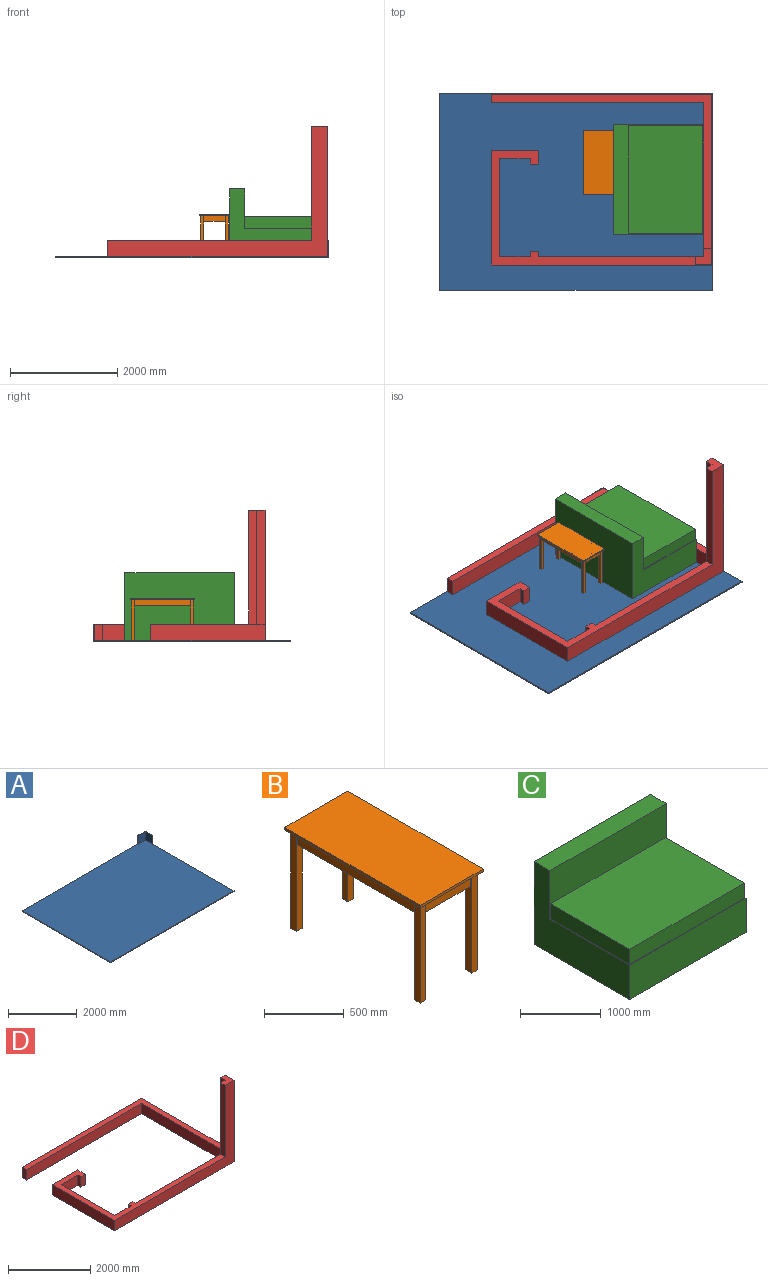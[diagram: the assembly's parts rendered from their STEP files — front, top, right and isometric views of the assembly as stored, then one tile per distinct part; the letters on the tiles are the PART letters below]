
ASSEMBLY  parts=4 mates=7
PART A: 11 faces, bbox 5080x3657.6x330.2 mm
  f0: plane 5080x330.2mm, normal (0,1,0), area 221935mm2, adj f1,f3,f4,f5,f6,f10
  f1: plane 3657.6x25.4mm, normal (-1,0,0), area 92903mm2, adj f0,f2,f4,f5
  f2: plane 5080x25.4mm, normal (0,-1,0), area 129032mm2, adj f1,f3,f4,f5
  f3: plane 3657.6x330.2mm, normal (1,0,0), area 185806.1mm2, adj f0,f2,f4,f5,f9,f10
  f4: plane 5080x3657.6mm, normal (0,0,1), area 18573027.4mm2, adj f0,f1,f2,f3,f6,f7,f8,f9
  f5: plane 5080x3657.6mm, normal (0,0,-1), area 18580608mm2, adj f0,f1,f2,f3
  f6: plane 304.8x12.7mm, normal (-1,0,0), area 3871mm2, adj f0,f4,f7,f10
  f7: plane 304.8x292.1mm, normal (0,-1,0), area 89032.1mm2, adj f4,f6,f8,f10
  f8: plane 304.8x292.1mm, normal (-1,0,0), area 89032.1mm2, adj f4,f7,f9,f10
  f9: plane 304.8x12.7mm, normal (0,-1,0), area 3871mm2, adj f3,f4,f8,f10
  f10: plane 304.8x304.8mm, normal (0,0,1), area 7580.6mm2, adj f0,f3,f6,f7,f8,f9
PART B: 39 faces, bbox 558.8x1200.2x774.7 mm
  f0: plane 1200.15x558.8mm, normal (0,0,-1), area 123709.4mm2, adj f2,f3,f4,f5,f7,f10,f13,f16
  f1: plane 1073.15x431.8mm, normal (0,0,-1), area 462741mm2, adj f8,f11,f14,f17,f19,f22,f24,f25
  f2: plane 558.8x19.05mm, normal (0,1,0), area 10645.1mm2, adj f0,f3,f5,f6
  f3: plane 1200.15x19.05mm, normal (-1,0,0), area 22862.9mm2, adj f0,f2,f4,f6
  f4: plane 558.8x19.05mm, normal (0,-1,0), area 10645.1mm2, adj f0,f3,f5,f6
  f5: plane 1200.15x19.05mm, normal (1,0,0), area 22862.9mm2, adj f0,f2,f4,f6
  f6: plane 1200.15x558.8mm, normal (0,0,1), area 670643.8mm2, adj f2,f3,f4,f5
  f7: plane 1047.75x95.25mm, normal (-1,0,0), area 99798.2mm2, adj f0,f9,f25,f34
  f8: plane 1047.75x95.25mm, normal (1,0,0), area 99798.2mm2, adj f1,f9,f25,f34
  f9: plane 1047.75x25.4mm, normal (0,0,-1), area 26612.9mm2, adj f7,f8,f25,f34
  f10: plane 406.4x95.25mm, normal (0,-1,0), area 38709.6mm2, adj f0,f12,f22,f24
  f11: plane 406.4x95.25mm, normal (0,1,0), area 38709.6mm2, adj f1,f12,f22,f24
  f12: plane 406.4x25.4mm, normal (0,0,-1), area 10322.6mm2, adj f10,f11,f22,f24
  f13: plane 1047.75x95.25mm, normal (1,0,0), area 99798.2mm2, adj f0,f15,f19,f32
  f14: plane 1047.75x95.25mm, normal (-1,0,0), area 99798.2mm2, adj f1,f15,f19,f32
  f15: plane 1047.75x25.4mm, normal (0,0,-1), area 26612.8mm2, adj f13,f14,f19,f32
  f16: plane 406.4x95.25mm, normal (0,1,0), area 38709.6mm2, adj f0,f18,f29,f37
  f17: plane 406.4x95.25mm, normal (0,-1,0), area 38709.6mm2, adj f1,f18,f29,f37
  f18: plane 406.4x25.4mm, normal (0,0,-1), area 10322.6mm2, adj f16,f17,f29,f37
  f19: plane 755.65x50.8mm, normal (0,1,0), area 35967.7mm2, adj f0,f1,f13,f14,f15,f20,f22,f23
  f20: plane 755.65x50.8mm, normal (1,0,0), area 38387mm2, adj f0,f19,f21,f23
  f21: plane 755.65x50.8mm, normal (0,-1,0), area 38387mm2, adj f0,f20,f22,f23
  f22: plane 755.65x50.8mm, normal (-1,0,0), area 35967.7mm2, adj f0,f1,f10,f11,f12,f19,f21,f23
  f23: plane 50.8x50.8mm, normal (0,0,-1), area 2580.6mm2, adj f19,f20,f21,f22
  f24: plane 755.65x50.8mm, normal (1,0,0), area 35967.7mm2, adj f0,f1,f10,f11,f12,f25,f26,f28
  f25: plane 755.65x50.8mm, normal (0,1,0), area 35967.7mm2, adj f0,f1,f7,f8,f9,f24,f27,f28
  f26: plane 755.65x50.8mm, normal (0,-1,0), area 38387mm2, adj f0,f24,f27,f28
  f27: plane 755.65x50.8mm, normal (-1,0,0), area 38387mm2, adj f0,f25,f26,f28
  f28: plane 50.8x50.8mm, normal (0,0,-1), area 2580.6mm2, adj f24,f25,f26,f27
  f29: plane 755.65x50.8mm, normal (-1,0,0), area 35967.7mm2, adj f0,f1,f16,f17,f18,f30,f32,f33
  f30: plane 755.65x50.8mm, normal (0,1,0), area 38387mm2, adj f0,f29,f31,f33
  f31: plane 755.65x50.8mm, normal (1,0,0), area 38387mm2, adj f0,f30,f32,f33
  f32: plane 755.65x50.8mm, normal (0,-1,0), area 35967.7mm2, adj f0,f1,f13,f14,f15,f29,f31,f33
  f33: plane 50.8x50.8mm, normal (0,0,-1), area 2580.6mm2, adj f29,f30,f31,f32
  f34: plane 755.65x50.8mm, normal (0,-1,0), area 35967.7mm2, adj f0,f1,f7,f8,f9,f35,f37,f38
  f35: plane 755.65x50.8mm, normal (-1,0,0), area 38387mm2, adj f0,f34,f36,f38
  f36: plane 755.65x50.8mm, normal (0,1,0), area 38387mm2, adj f0,f35,f37,f38
  f37: plane 755.65x50.8mm, normal (1,0,0), area 35967.7mm2, adj f0,f1,f16,f17,f18,f34,f36,f38
  f38: plane 50.8x50.8mm, normal (0,0,-1), area 2580.6mm2, adj f34,f35,f36,f37
PART C: 12 faces, bbox 2038.4x1676.4x1257.3 mm
  f0: plane 1676.4x1257.3mm, normal (-1,0,0), area 1078707.5mm2, adj f1,f2,f3,f5,f6,f7
  f1: plane 2038.35x520.7mm, normal (0,-1,0), area 1061368.8mm2, adj f0,f4,f5,f6
  f2: plane 2038.35x279.4mm, normal (0,0,1), area 569515mm2, adj f0,f3,f4,f7
  f3: plane 2038.35x1257.3mm, normal (0,1,0), area 2562817.5mm2, adj f0,f2,f4,f5
  f4: plane 1676.4x1257.3mm, normal (1,0,0), area 1078707.5mm2, adj f1,f2,f3,f5,f6,f7
  f5: plane 2038.35x1676.4mm, normal (0,0,-1), area 3417089.9mm2, adj f0,f1,f3,f4
  f6: plane 2038.35x1397mm, normal (0,0,1), area 61048.3mm2, adj f0,f1,f4,f7,f8,f9,f10
  f7: plane 2038.35x736.6mm, normal (0,-1,0), area 1041288.2mm2, adj f0,f2,f4,f6,f8,f10,f11
  f8: plane 1384.3x228.6mm, normal (-1,0,0), area 316451mm2, adj f6,f7,f9,f11
  f9: plane 2012.95x228.6mm, normal (0,-1,0), area 460160.4mm2, adj f6,f8,f10,f11
  f10: plane 1384.3x228.6mm, normal (1,0,0), area 316451mm2, adj f6,f7,f9,f11
  f11: plane 2012.95x1384.3mm, normal (0,0,1), area 2786526.7mm2, adj f7,f8,f9,f10
PART D: 24 faces, bbox 4102.1x3175x2425.7 mm
  f0: plane 3797.3x2133.6mm, normal (0,0,1), area 1021933.4mm2, adj f1,f2,f3,f4,f5,f6,f7,f8
  f1: plane 304.8x101.6mm, normal (-1,0,0), area 30967.7mm2, adj f0,f2,f18,f20
  f2: plane 571.5x304.8mm, normal (0,1,0), area 174193.2mm2, adj f0,f1,f3,f20
  f3: plane 1828.8x304.8mm, normal (1,0,0), area 557418.2mm2, adj f0,f2,f4,f20
  f4: plane 571.5x304.8mm, normal (0,-1,0), area 174193.2mm2, adj f0,f3,f5,f20
  f5: plane 304.8x101.6mm, normal (-1,0,0), area 30967.7mm2, adj f0,f4,f6,f20
  f6: plane 304.8x152.4mm, normal (0,-1,0), area 46451.5mm2, adj f0,f5,f7,f20
  f7: plane 304.8x254mm, normal (1,0,0), area 77419.2mm2, adj f0,f6,f8,f20
  f8: plane 876.3x304.8mm, normal (0,1,0), area 267096.2mm2, adj f0,f7,f9,f20
  f9: plane 2133.6x304.8mm, normal (-1,0,0), area 650321.3mm2, adj f0,f8,f10,f20
  f10: plane 4102.1x2425.7mm, normal (0,-1,0), area 1896770.4mm2, adj f0,f9,f11,f20,f21,f23
  f11: plane 3175x2425.7mm, normal (1,0,0), area 1614190.3mm2, adj f10,f12,f19,f20,f22,f23
  f12: plane 4102.1x304.8mm, normal (0,1,0), area 1250320.1mm2, adj f11,f13,f19,f20
  f13: plane 304.8x152.4mm, normal (-1,0,0), area 46451.5mm2, adj f12,f14,f19,f20
  f14: plane 3949.7x304.8mm, normal (0,-1,0), area 1203868.6mm2, adj f13,f15,f19,f20
  f15: plane 2870.2x2425.7mm, normal (-1,0,0), area 1198062.1mm2, adj f14,f16,f19,f20,f22,f23
  f16: plane 3073.4x2425.7mm, normal (0,1,0), area 1259997.5mm2, adj f0,f15,f17,f20,f21,f23
  f17: plane 304.8x101.6mm, normal (1,0,0), area 30967.7mm2, adj f0,f16,f18,f20
  f18: plane 304.8x152.4mm, normal (0,1,0), area 46451.5mm2, adj f0,f1,f17,f20
  f19: plane 4102.1x2870.2mm, normal (0,0,1), area 1039352.8mm2, adj f11,f12,f13,f14,f15,f22
  f20: plane 4102.1x3175mm, normal (0,0,-1), area 2130963.5mm2, adj f1,f2,f3,f4,f5,f6,f7,f8
  f21: plane 2120.9x152.4mm, normal (-1,0,0), area 323225.2mm2, adj f0,f10,f16,f23
  f22: plane 2120.9x152.4mm, normal (0,1,0), area 323225.2mm2, adj f11,f15,f19,f23
  f23: plane 304.8x304.8mm, normal (0,0,1), area 69677.3mm2, adj f10,f11,f15,f16,f21,f22
PLACE A t=(1937.26,1323.05,-189.92)mm
PLACE B t=(4823.09,5967.48,591.13)mm
PLACE C rot(axis=(0,0,1),90deg) t=(4931.8,6166.15,-164.52)mm
PLACE D t=(-1905,0,-164.52)mm
MATE planar C.f1 <-> D.f15  axis (1,0,0) through (6819.48,6069.16,95.83)mm
MATE planar A.f8 <-> D.f11  axis (-1,0,0) through (6971.88,7510.61,140.28)mm
MATE planar B.f5 <-> C.f3  axis (1,0,0) through (5143.08,6389.12,600.66)mm
MATE planar C.f5 <-> A.f4  axis (0,0,-1) through (5981.28,6069.16,-164.52)mm
MATE planar B.f28 <-> A.f4  axis (0,0,-1) through (4635.08,5839.85,-164.52)mm
MATE planar A.f4 <-> D.f20  axis (0,0,1) through (4443.58,5839.85,-164.52)mm
MATE planar A.f7 <-> D.f12  axis (0,-1,0) through (6825.83,7656.66,-12.12)mm
